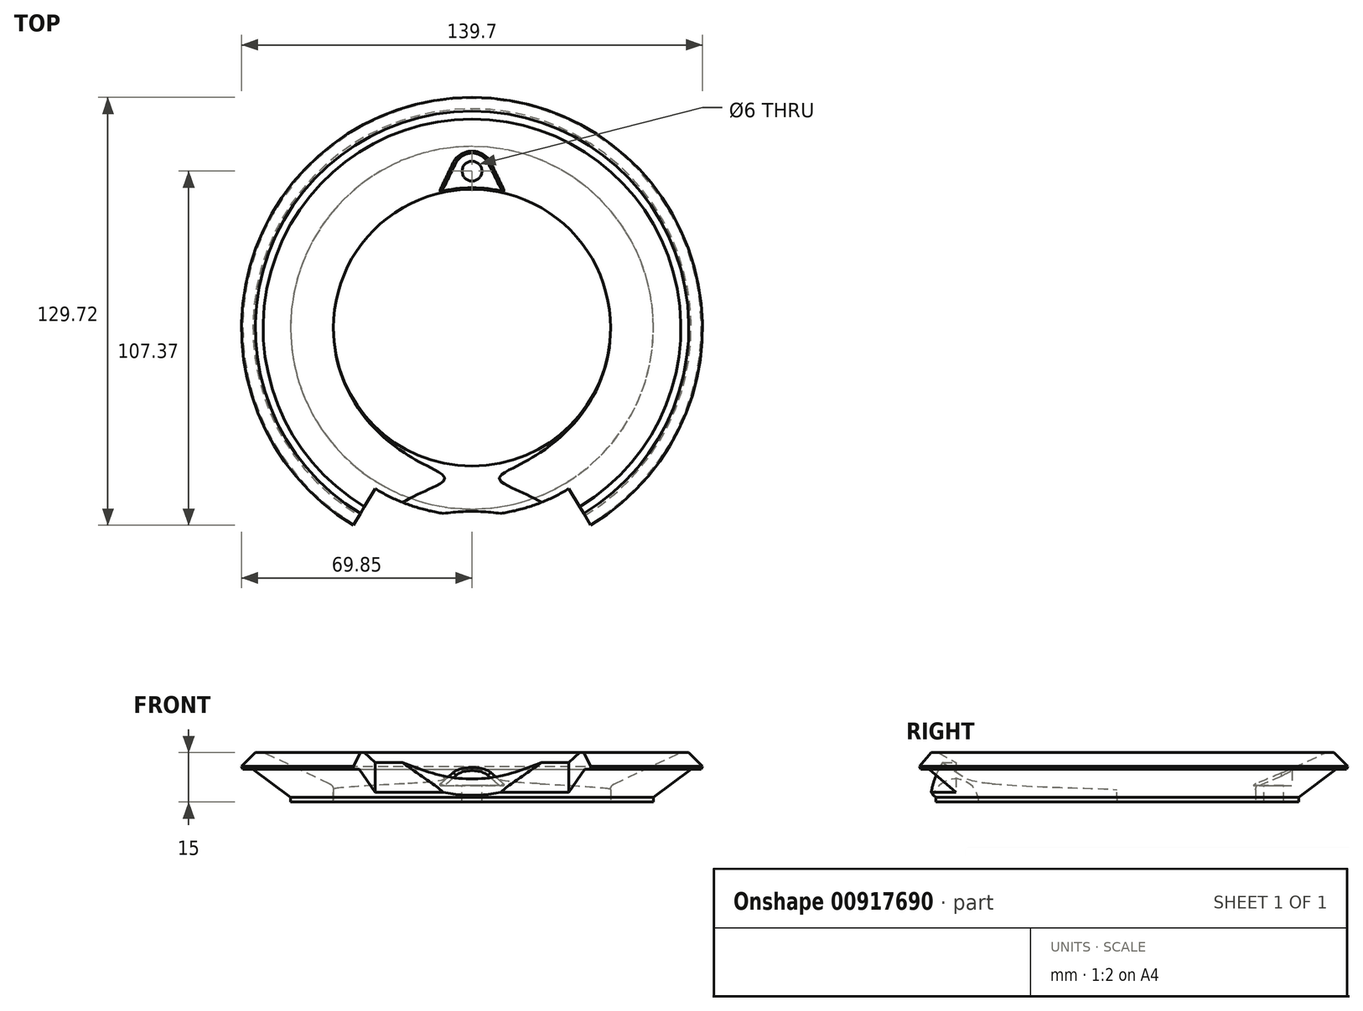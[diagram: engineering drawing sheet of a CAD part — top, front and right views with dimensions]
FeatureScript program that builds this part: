
annotation { "Feature Type Name" : "Feature", "Feature Type Description" : "" }
export const myFeature = defineFeature(function(context is Context, id is Id, definition is map)
    precondition{}
    {
        {
            assignVariable(context, id + "F0", {"name" : "tank_cap_notch_enable", "anyValue" : 1});
        }
        {
            assignVariable(context, id + "F1", {"name" : "bolt_plane_height", "anyValue" : 5});
        }
        {
            var Q0;
            Q0=qCreatedBy(makeId("Front.planeOp"),FACE);
            var sketch = newSketch(context, id + "F2", { "sketchPlane" : qUnion([Q0])});
            skLineSegment(sketch, "E0", {"start": v(-42, 0) * mm, "end": v(-55, 0) * mm});
            skLineSegment(sketch, "E1", {"start": v(-55, 0) * mm, "end": v(-55, 1.5) * mm});
            skLineSegment(sketch, "E2", {"start": v(-55, 1.5) * mm, "end": v(-66.4, 10) * mm});
            skLineSegment(sketch, "E3", {"start": v(-66.4, 10) * mm, "end": v(-69.5, 10) * mm});
            skLineSegment(sketch, "E4", {"start": v(-65.7, 15) * mm, "end": v(-63.3, 15) * mm});
            skLineSegment(sketch, "E5", {"start": v(-63.3, 15) * mm, "end": v(-42, 5) * mm});
            skLineSegment(sketch, "E6", {"start": v(-42, 5) * mm, "end": v(-42, 0) * mm});
            skLineSegment(sketch, "E7", {"start": v(-69.5, 10) * mm, "end": v(-69.85, 10.85) * mm});
            skLineSegment(sketch, "E8", {"start": v(-69.85, 10.85) * mm, "end": v(-65.7, 15) * mm});
            skLineSegment(sketch, "E9", {"start": v(0, 0) * mm, "end": v(0, 12.4) * mm});
            skSolve(sketch);
        }
        {
            var Q0;
            Q0=makeQuery(id+"F2.imprint","IMPRINT",FACE,{"disambiguationData":[TD([[makeQuery(id+"F2.imprint","IMPRINT",EDGE,{"derivedFrom":sQuery(id+"F2.wireOp",EDGE,"E0")}),-1.0]])]});
            var Q1;
            Q1=sQuery(id+"F2.wireOp",EDGE,"E9");
            revolve(context, id + "F3", {"surfaceOperationType" : NewSurfaceOperationType.NEW, "entities" : qUnion([Q0]), "axis" : qUnion([Q1]), "revolveType" : RevolveType.FULL});
        }
        {
            var Q0;
            Q0=makeQuery(id+"F3.opRevolve","SWEPT_EDGE",EDGE,{"disambiguationData":[OSD([sQuery(id+"F2.wireOp",EDGE,"E5"),sQuery(id+"F2.wireOp",EDGE,"E6")])]});
            fillet(context, id + "F4", {"entities" : qUnion([Q0]), "radius" : 2 * mm, "tangentPropagation" : true, "allowEdgeOverflow" : false});
        }
        {
            var Q0;
            Q0=qCreatedBy(makeId("Top.planeOp"),FACE);
            cPlane(context, id + "F5", {"entities" : qUnion([Q0]), "cplaneType" : CPlaneType.OFFSET, "offset" : (getVariable(context, 'bolt_plane_height')) * mm, "width" : 150 * mm, "height" : 150 * mm});
        }
        {
            var Q0;
            Q0=qCreatedBy(id+"F5.planeOp",FACE);
            var sketch = newSketch(context, id + "F6", { "sketchPlane" : qUnion([Q0])});
            skLineSegment(sketch, "E10", {"start": v(0, 0) * mm, "end": v(0, 47.5) * mm});
            skLineSegment(sketch, "E11", {"start": v(-15.4, 28.5) * mm, "end": v(15.4, 28.5) * mm});
            skLineSegment(sketch, "E12", {"start": v(-15.4, 28.5) * mm, "end": v(-4.94, 49.91) * mm});
            skLineSegment(sketch, "E13", {"start": v(15.4, 28.5) * mm, "end": v(4.94, 49.91) * mm});
            skArc(sketch, "E14", {"start": v(-4.94, 49.91) * mm, "mid": v(0, 42) * mm, "end": v(4.94, 49.91) * mm, "construction": true});
            skArc(sketch, "E15", {"start": v(4.94, 49.91) * mm, "mid": v(0, 53) * mm, "end": v(-4.94, 49.91) * mm});
            skSolve(sketch);
        }
        {
            var Q0;
            {var subQ0=sQuery(id+"F6.wireOp",EDGE,"E12");Q0=makeQuery(id+"F6.imprint","IMPRINT",FACE,{"disambiguationData":[TD([[makeQuery(id+"F6.imprint","IMPRINT",EDGE,{"derivedFrom":subQ0}),-1.0]])]});}
            extrude(context, id + "F7", {"entities" : qUnion([Q0]), "operationType" : NewBodyOperationType.REMOVE, "endBound" : BoundingType.THROUGH_ALL, "depth" : 25 * mm, "offsetDistance" : 25 * mm});
        }
        {
            var Q0;
            Q0=makeQuery(id+"F7.boolean.opBoolean","INTERSECT",EDGE,{"derivedFrom":[makeQuery(id+"F3.opRevolve","SWEPT_FACE",FACE,{"disambiguationData":[OSD([sQuery(id+"F2.wireOp",EDGE,"E5")])]}),makeQuery(id+"F7.opExtrude","SWEPT_FACE",FACE,{"disambiguationData":[OSD([sQuery(id+"F6.wireOp",EDGE,"E13")])]})]});
            var Q1;
            Q1=makeQuery(id+"F7.boolean.opBoolean","INTERSECT",EDGE,{"derivedFrom":[makeQuery(id+"F3.opRevolve","SWEPT_FACE",FACE,{"disambiguationData":[OSD([sQuery(id+"F2.wireOp",EDGE,"E5")])]}),makeQuery(id+"F7.opExtrude","SWEPT_FACE",FACE,{"disambiguationData":[OSD([sQuery(id+"F6.wireOp",EDGE,"E15")])]})]});
            var Q2;
            Q2=makeQuery(id+"F7.boolean.opBoolean","INTERSECT",EDGE,{"derivedFrom":[makeQuery(id+"F3.opRevolve","SWEPT_FACE",FACE,{"disambiguationData":[OSD([sQuery(id+"F2.wireOp",EDGE,"E5")])]}),makeQuery(id+"F7.opExtrude","SWEPT_FACE",FACE,{"disambiguationData":[OSD([sQuery(id+"F6.wireOp",EDGE,"E12")])]})]});
            fillet(context, id + "F8", {"entities" : qUnion([Q0, Q1, Q2]), "radius" : 1 * mm, "tangentPropagation" : true, "allowEdgeOverflow" : false});
        }
        {
            var Q0;
            Q0=qCreatedBy(id+"F5.planeOp",FACE);
            var sketch = newSketch(context, id + "F9", { "sketchPlane" : qUnion([Q0])});
            skCircle(sketch, "E16", {"center": v(0, 47.5) * mm, "radius": 3 * mm});
            skLineSegment(sketch, "E17", {"start": v(0, 0) * mm, "end": v(0, 47.5) * mm});
            skSolve(sketch);
        }
        {
            var Q0;
            Q0=makeQuery(id+"F9.imprint","IMPRINT",FACE,{"disambiguationData":[TD([[makeQuery(id+"F9.imprint","IMPRINT",EDGE,{"derivedFrom":sQuery(id+"F9.wireOp",EDGE,"E16")}),1.0]])]});
            extrude(context, id + "F10", {"entities" : qUnion([Q0]), "operationType" : NewBodyOperationType.REMOVE, "endBound" : BoundingType.THROUGH_ALL, "oppositeDirection" : true, "depth" : 25 * mm, "offsetDistance" : 25 * mm});
        }
        {
            var Q0;
            Q0=qCreatedBy(makeId("Front.planeOp"),FACE);
            var sketch = newSketch(context, id + "F11", { "sketchPlane" : qUnion([Q0])});
            skLineSegment(sketch, "E18", {"start": v(0, 0) * mm, "end": v(0, 39.57) * mm});
            skSolve(sketch);
        }
        {
            var Q0;
            Q0=qCreatedBy(makeId("Right.planeOp"),FACE);
            var sketch = newSketch(context, id + "F12", { "sketchPlane" : qUnion([Q0])});
            skLineSegment(sketch, "E19.bottom", {"start": v(-75, 20) * mm, "end": v(-57, 20) * mm});
            skLineSegment(sketch, "E19.top", {"start": v(-75, 0) * mm, "end": v(-57, 0) * mm});
            skLineSegment(sketch, "E19.left", {"start": v(-75, 20) * mm, "end": v(-75, 0) * mm});
            skLineSegment(sketch, "E19.right", {"start": v(-57, 20) * mm, "end": v(-57, 0) * mm});
            skLineSegment(sketch, "E20", {"start": v(0, 0) * mm, "end": v(0, 34.37) * mm});
            skSolve(sketch);
        }
        {
            var Q0;
            Q0=makeQuery(id+"F12.imprint","IMPRINT",FACE,{"disambiguationData":[TD([[makeQuery(id+"F12.imprint","IMPRINT",EDGE,{"derivedFrom":sQuery(id+"F12.wireOp",EDGE,"E19.bottom")}),-1.0]])]});
            var Q1;
            Q1=sQuery(id+"F12.wireOp",EDGE,"E20");
            revolve(context, id + "F13", {"operationType" : NewBodyOperationType.REMOVE, "surfaceOperationType" : NewSurfaceOperationType.NEW, "entities" : qUnion([Q0]), "axis" : qUnion([Q1]), "revolveType" : RevolveType.SYMMETRIC, "angle" : 62 * degree});
        }
        {
            var Q0;
            Q0=qCreatedBy(makeId("Top.planeOp"),FACE);
            var sketch = newSketch(context, id + "F14", { "sketchPlane" : qUnion([Q0])});
            skCircle(sketch, "E21", {"center": v(0, 0) * mm, "radius": 42 * mm});
            skLineSegment(sketch, "E22", {"start": v(-49.45, -49) * mm, "end": v(41.22, -49) * mm});
            skSolve(sketch);
        }
        {
            var Q0;
            Q0=makeQuery(id+"F14.imprint","IMPRINT",FACE,{"disambiguationData":[TD([[makeQuery(id+"F14.imprint","IMPRINT",EDGE,{"derivedFrom":sQuery(id+"F14.wireOp",EDGE,"E21")}),1.0]])]});
            var Q1;
            Q1=sQuery(id+"F14.wireOp",EDGE,"E22");
            revolve(context, id + "F15", {"operationType" : NewBodyOperationType.REMOVE, "surfaceOperationType" : NewSurfaceOperationType.NEW, "entities" : qUnion([Q0]), "axis" : qUnion([Q1]), "revolveType" : RevolveType.ONE_DIRECTION, "angle" : (getVariable(context, 'tank_cap_notch_enable') * 180) * degree});
        }
    });
